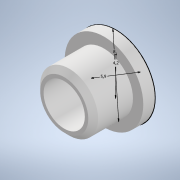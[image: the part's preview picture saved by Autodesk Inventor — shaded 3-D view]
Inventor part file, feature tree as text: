
AUTODESK INVENTOR PART (.ipt)
format: ipt  version: 2022 (Build 260153000, 153)  size: 126,464 bytes
history: native  units: mm
features: sketch x3, extrude x2, other x1, chamfer x1
ambient origin geometry x8: Origin, YZ Plane, XZ Plane, XY Plane, X Axis, Y Axis, Z Axis, Center Point
bodies: Body1 (feature_tree)
feature tree (7):
  other  "Твердое тело1"
  sketch  "Эскиз1"
  extrude  "Выдавливание1"  Depth=5.9mm
  extrude  "Выдавливание3"  Depth=4.2mm
  chamfer  "Фаска1"  Distance=8.0mm
  sketch  "Эскиз2"
  sketch  "Эскиз4"
